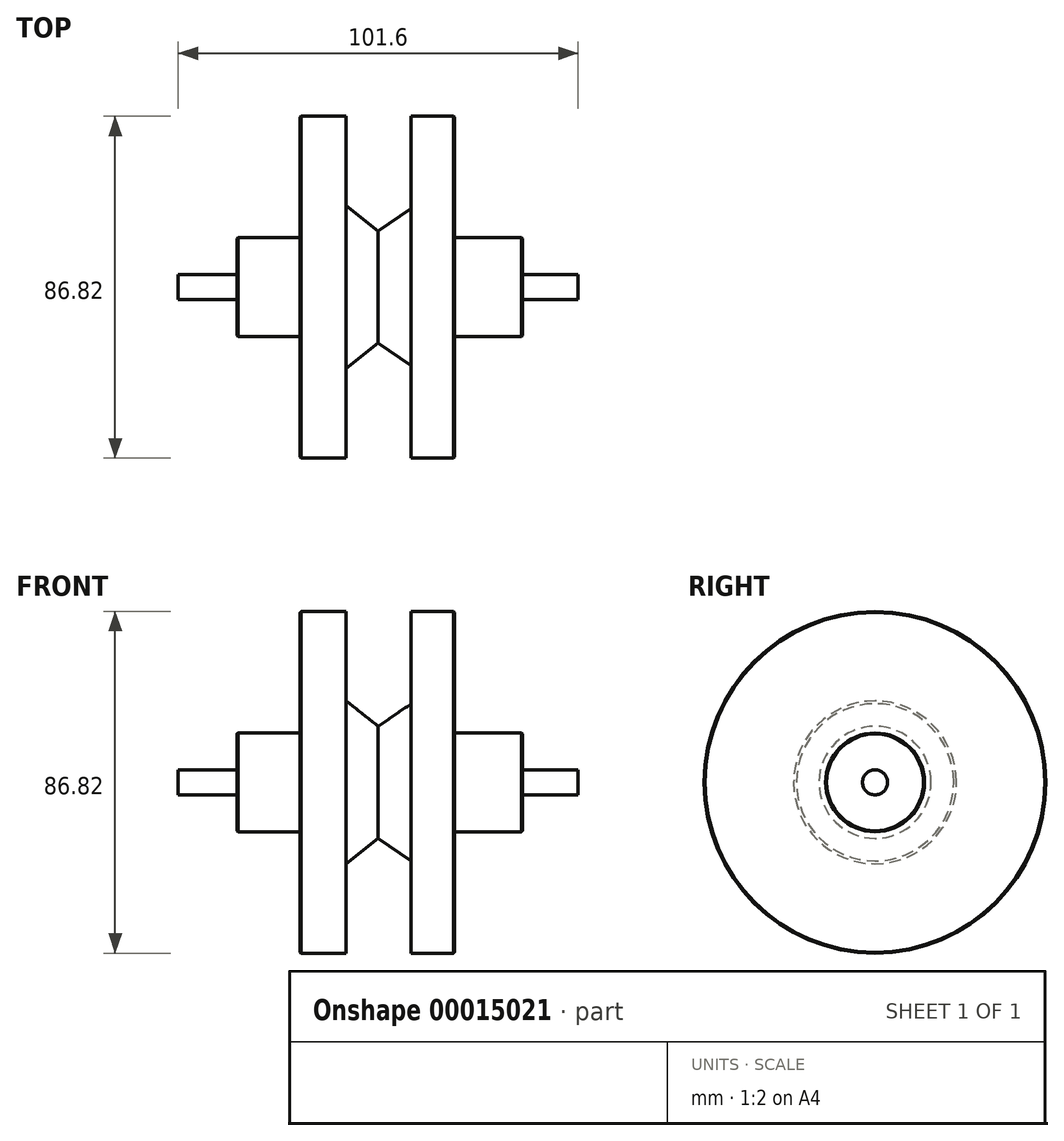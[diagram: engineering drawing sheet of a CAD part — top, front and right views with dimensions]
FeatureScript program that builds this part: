
annotation { "Feature Type Name" : "Feature", "Feature Type Description" : "" }
export const myFeature = defineFeature(function(context is Context, id is Id, definition is map)
    precondition{}
    {
        {
            var Q0;
            Q0=qCreatedBy(makeId("Front.planeOp"),FACE);
            var sketch = newSketch(context, id + "F0", { "sketchPlane" : qUnion([Q0])});
            skLineSegment(sketch, "E0", {"start": v(-100.46, 0) * mm, "end": v(100.7, 0) * mm});
            skLineSegment(sketch, "E1", {"start": v(-35.88, 0) * mm, "end": v(-35.88, 12.56) * mm});
            skLineSegment(sketch, "E2", {"start": v(-35.88, 12.56) * mm, "end": v(-19.85, 12.56) * mm});
            skLineSegment(sketch, "E3", {"start": v(-19.85, 12.56) * mm, "end": v(-19.85, 43.41) * mm});
            skLineSegment(sketch, "E4", {"start": v(-19.85, 43.41) * mm, "end": v(-8.13, 43.41) * mm});
            skLineSegment(sketch, "E5", {"start": v(-8.13, 43.41) * mm, "end": v(-8.13, 20.7) * mm});
            skLineSegment(sketch, "E6", {"start": v(-8.13, 20.7) * mm, "end": v(0, 14.23) * mm});
            skLineSegment(sketch, "E7", {"start": v(0, 14.23) * mm, "end": v(8.37, 19.97) * mm});
            skLineSegment(sketch, "E8", {"start": v(8.37, 19.97) * mm, "end": v(8.37, 43.41) * mm});
            skLineSegment(sketch, "E9", {"start": v(8.37, 43.41) * mm, "end": v(19.37, 43.41) * mm});
            skLineSegment(sketch, "E10", {"start": v(19.37, 43.41) * mm, "end": v(19.37, 12.56) * mm});
            skLineSegment(sketch, "E11", {"start": v(19.37, 12.56) * mm, "end": v(36.6, 12.56) * mm});
            skLineSegment(sketch, "E12", {"start": v(36.6, 12.56) * mm, "end": v(36.6, 0) * mm});
            skSolve(sketch);
        }
        {
            var Q0;
            Q0=qCreatedBy(makeId("Right.planeOp"),FACE);
            var sketch = newSketch(context, id + "F1", { "sketchPlane" : qUnion([Q0])});
            skCircle(sketch, "E13", {"center": v(0, 0) * mm, "radius": 3.18 * mm});
            skSolve(sketch);
        }
        {
            var Q0;
            Q0=makeQuery(id+"F1.imprint","IMPRINT",FACE,{"disambiguationData":[TD([[makeQuery(id+"F1.imprint","IMPRINT",EDGE,{"derivedFrom":sQuery(id+"F1.wireOp",EDGE,"E13")}),1.0]])]});
            extrude(context, id + "F2", {"entities" : qUnion([Q0]), "endBound" : BoundingType.SYMMETRIC, "depth" : 101.6 * mm});
        }
        {
            var Q0;
            {var subQ1=sQuery(id+"F0.wireOp",EDGE,"E1");Q0=makeQuery(id+"F0.imprint","IMPRINT",FACE,{"disambiguationData":[TD([[makeQuery(id+"F0.imprint","IMPRINT",EDGE,{"derivedFrom":subQ1}),-1.0]])]});}
            var Q1;
            Q1=sQuery(id+"F0.wireOp",EDGE,"E0");
            revolve(context, id + "F3", {"operationType" : NewBodyOperationType.ADD, "entities" : qUnion([Q0]), "axis" : qUnion([Q1]), "revolveType" : RevolveType.FULL});
        }
        {
            var Q0;
            Q0=makeQuery(id+"F3.opRevolve","SWEPT_EDGE",EDGE,{"disambiguationData":[OSD([sQuery(id+"F0.wireOp",EDGE,"E3"),sQuery(id+"F0.wireOp",EDGE,"E4")])]});
            var Q1;
            Q1=makeQuery(id+"F3.opRevolve","SWEPT_EDGE",EDGE,{"disambiguationData":[OSD([sQuery(id+"F0.wireOp",EDGE,"E1"),sQuery(id+"F0.wireOp",EDGE,"E2")])]});
            var Q2;
            Q2=makeQuery(id+"F3.opRevolve","SWEPT_EDGE",EDGE,{"disambiguationData":[OSD([sQuery(id+"F0.wireOp",EDGE,"E11"),sQuery(id+"F0.wireOp",EDGE,"E12")])]});
            var Q3;
            Q3=makeQuery(id+"F3.opRevolve","SWEPT_EDGE",EDGE,{"disambiguationData":[OSD([sQuery(id+"F0.wireOp",EDGE,"E9"),sQuery(id+"F0.wireOp",EDGE,"E10")])]});
            chamfer(context, id + "F4", {"entities" : qUnion([Q0, Q1, Q2, Q3]), "width" : 0.25 * mm, "tangentPropagation" : true});
        }
    });
